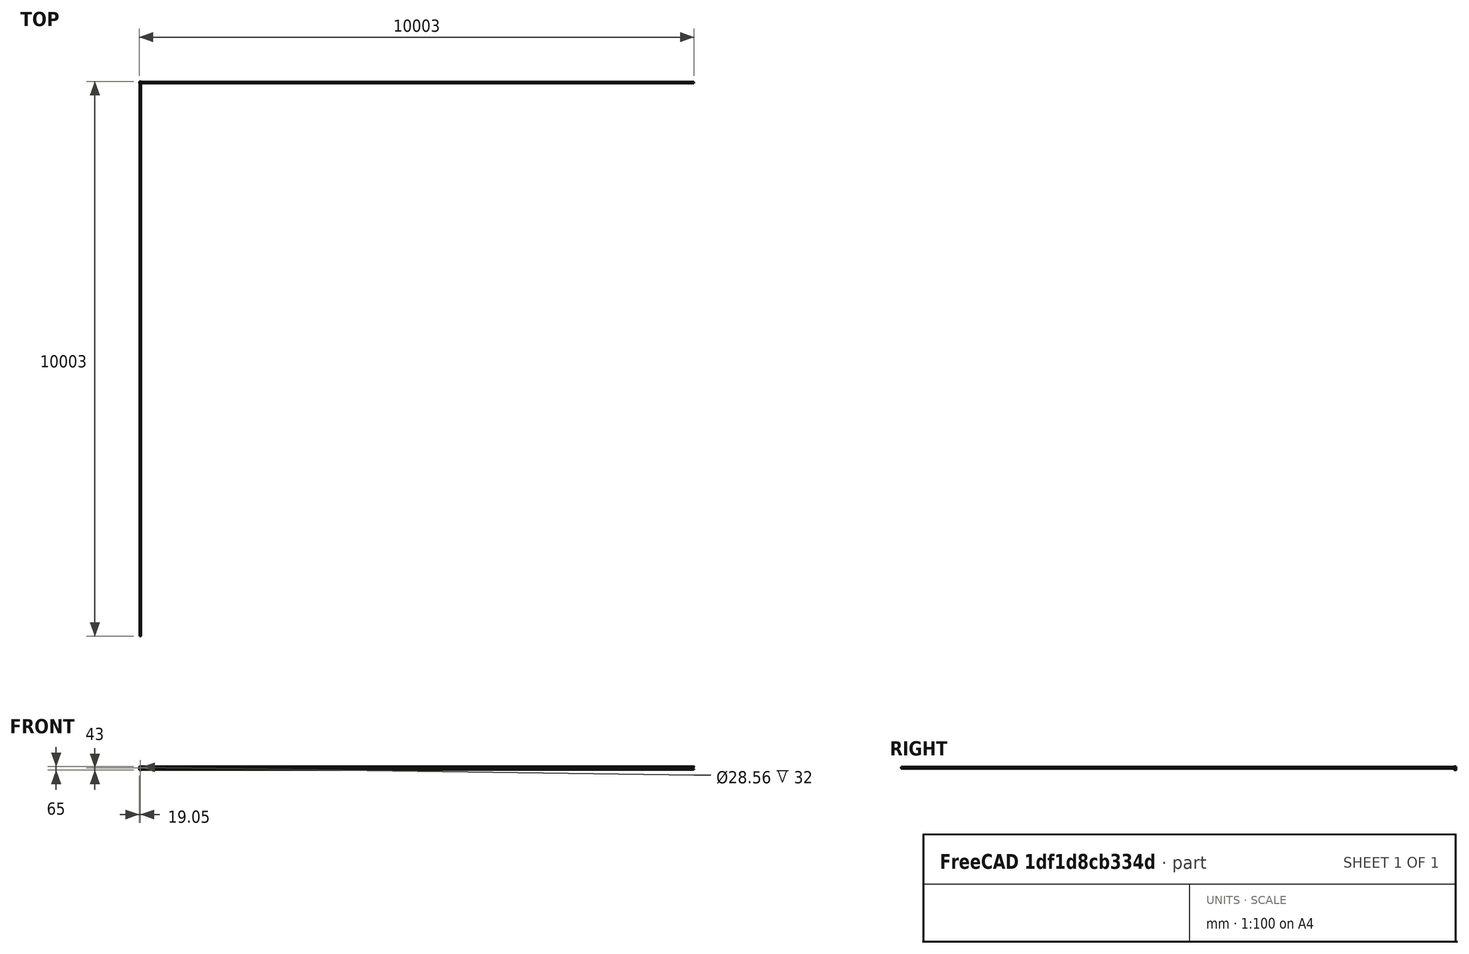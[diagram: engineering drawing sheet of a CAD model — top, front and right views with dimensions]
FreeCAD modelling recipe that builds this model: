
FCSTD DOCUMENT  (FreeCAD 0.16R)
Label: Stem
License: All rights reserved
LicenseURL: http://en.wikipedia.org/wiki/All_rights_reserved
objects: Sketcher::SketchObject×7, PartDesign::Pocket×6, PartDesign::Mirrored×2, PartDesign::Pad×1, Mesh::Feature×1
note: 23 computed .brp shape members not serialized (recipe doc carries the construction recipe); baked Part::Feature solids carry a one-line shape summary decoded from their .brp

FEATURE [Sketcher::SketchObject] Sketch
  sketch-geometry (1):
    g0: Circle CenterX=0 CenterY=0 CenterZ=0 NormalX=0 NormalY=0 NormalZ=1 Radius=19.05
  constraints (2):
    c: Coincident(g0,g-1)
    c: Radius(g0) = 19.05
FEATURE [PartDesign::Pad] Pad  label="RawStock"
  Length = 65
  Length2 = 100
  Sketch = -> Sketch
  Type = 0
FEATURE [Sketcher::SketchObject] Sketch001
  Placement = pos=(0,0,65) rot=(0,0,1;0rad)
  Support = -> Pad [Face3]
  sketch-geometry (4):
    g0: LineSegment StartX=-30 StartY=16 StartZ=0 EndX=30 EndY=16 EndZ=0
    g1: LineSegment StartX=30 StartY=16 StartZ=0 EndX=30 EndY=36 EndZ=0
    g2: LineSegment StartX=30 StartY=36 StartZ=0 EndX=-30 EndY=36 EndZ=0
    g3: LineSegment StartX=-30 StartY=36 StartZ=0 EndX=-30 EndY=16 EndZ=0
  constraints (12):
    c: Coincident(g0,g1)
    c: Coincident(g1,g2)
    c: Coincident(g2,g3)
    c: Coincident(g3,g0)
    c: Horizontal(g0)
    c: Horizontal(g2)
    c: Vertical(g1)
    c: Vertical(g3)
    c: DistanceY(g0) = 16
    c: Distance(g0) = 60
    c: DistanceX(g0) = -30
    c: DistanceY(g3,g3) = 20
FEATURE [PartDesign::Pocket] Pocket  label="TopCut"
  Length = 5
  Sketch = -> Sketch001
  Type = 1
FEATURE [PartDesign::Mirrored] Mirrored
  MirrorPlane = -> Sketch001 [H_Axis]
  Originals = -> [Pocket]
FEATURE [Sketcher::SketchObject] Sketch002
  ExternalGeometry = -> [Mirrored]
  Placement = pos=(0,16,0) rot=(0,0.707107,0.707107;3.14159rad)
  Support = -> Mirrored [Face3]
  sketch-geometry (1):
    g0: Circle CenterX=0 CenterY=43 CenterZ=0 NormalX=0 NormalY=0 NormalZ=1 Radius=14.28
  constraints (3):
    c: PointOnObject(g0,g-2)
    c: Radius(g0) = 14.28
    c: DistanceY(g0) = 43
FEATURE [PartDesign::Pocket] Pocket001  label="SteerHole"
  Length = 5
  Sketch = -> Sketch002
  Type = 1
FEATURE [Sketcher::SketchObject] Sketch003
  Placement = pos=(0,0,65) rot=(0,0,1;0rad)
  Support = -> Pocket001 [Face6]
  sketch-geometry (4):
    g0: LineSegment StartX=41 StartY=20 StartZ=0 EndX=16 EndY=20 EndZ=0
    g1: LineSegment StartX=16 StartY=20 StartZ=0 EndX=16 EndY=-20 EndZ=0
    g2: LineSegment StartX=16 StartY=-20 StartZ=0 EndX=41 EndY=-20 EndZ=0
    g3: LineSegment StartX=41 StartY=-20 StartZ=0 EndX=41 EndY=20 EndZ=0
  constraints (12):
    c: Coincident(g0,g1)
    c: Coincident(g1,g2)
    c: Coincident(g2,g3)
    c: Coincident(g3,g0)
    c: Horizontal(g0)
    c: Horizontal(g2)
    c: Vertical(g1)
    c: Vertical(g3)
    c: DistanceX(g-2,g1) = 16
    c: DistanceX(g0,g0) = 25
    c: Symmetric(g1,g0,g-1)
    c: DistanceY(g3,g3) = 40
FEATURE [PartDesign::Pocket] Pocket002  label="SideCutt"
  Length = 5
  Sketch = -> Sketch003
  Type = 1
FEATURE [PartDesign::Mirrored] Mirrored001
  MirrorPlane = -> Sketch003 [V_Axis]
  Originals = -> [Pocket002]
FEATURE [Sketcher::SketchObject] Sketch004
  ExternalGeometry = -> [Mirrored001]
  Placement = pos=(-16,0,0) rot=(0.57735,-0.57735,-0.57735;2.0944rad)
  Support = -> Mirrored001 [Face11]
  sketch-geometry (1):
    g0: Circle CenterX=0 CenterY=17.1503 CenterZ=0 NormalX=0 NormalY=0 NormalZ=1 Radius=11.1
  constraints (3):
    c: PointOnObject(g0,g-2)
    c: Radius(g0) = 11.1
    c: DistanceY(g0,g-4) = 16
FEATURE [PartDesign::Pocket] Pocket003  label="barhole"
  Length = 5
  Sketch = -> Sketch004
  Type = 1
FEATURE [Sketcher::SketchObject] Sketch005
  ExternalGeometry = -> [Pocket003]
  Placement = pos=(-16,0,0) rot=(0.57735,-0.57735,-0.57735;2.0944rad)
  Support = -> Pocket003 [Face16]
  sketch-geometry (1):
    g0: Circle CenterX=0 CenterY=61.5 CenterZ=0 NormalX=0 NormalY=0 NormalZ=1 Radius=2.5
  constraints (3):
    c: PointOnObject(g0,g-2)
    c: Radius(g0) = 2.5
    c: Distance(g0,g-3) = 3.5
FEATURE [PartDesign::Pocket] Pocket004  label="steerbolt"
  Length = 5
  Sketch = -> Sketch005
  Type = 1
FEATURE [Sketcher::SketchObject] Sketch008
  Placement = pos=(0,0,0) rot=(1,0,0;3.14159rad)
  Support = -> Pocket004 [Face2]
  sketch-geometry (4):
    g0: Circle CenterX=6 CenterY=13.5 CenterZ=0 NormalX=0 NormalY=0 NormalZ=1 Radius=2
    g1: Circle CenterX=-6 CenterY=-13.5 CenterZ=0 NormalX=0 NormalY=0 NormalZ=1 Radius=2
    g2: Circle CenterX=-6 CenterY=13.5 CenterZ=0 NormalX=0 NormalY=0 NormalZ=1 Radius=2
    g3: Circle CenterX=6 CenterY=-13.5 CenterZ=0 NormalX=0 NormalY=0 NormalZ=1 Radius=2
  constraints (10):
    c: Radius(g0) = 2
    c: Radius(g1) = 2
    c: Radius(g2) = 2
    c: Radius(g3) = 2
    c: Symmetric(g0,g2,g-2)
    c: Symmetric(g3,g1,g-2)
    c: DistanceX(g2,g-1) = 6
    c: DistanceX(g-2,g1) = -6
    c: DistanceY(g2) = 13.5
    c: DistanceY(g1) = -13.5
FEATURE [PartDesign::Pocket] Pocket005  label="SteerBolts"
  Length = 15
  Sketch = -> Sketch008
  Type = 0
FEATURE [Mesh::Feature] Mesh  label="SteerBolts (Meshed)"
